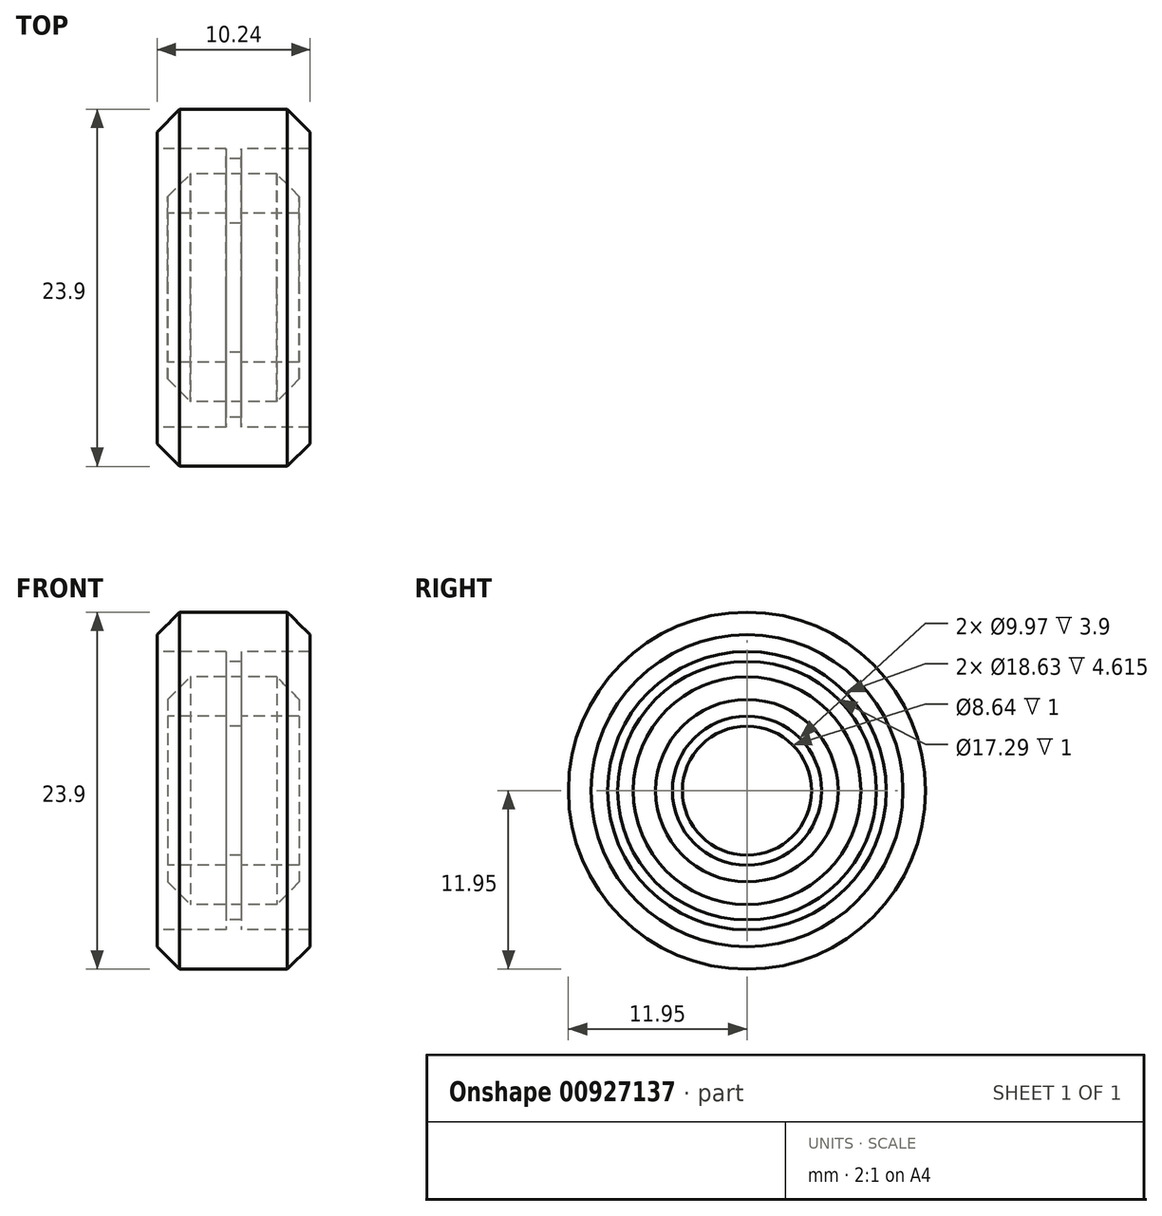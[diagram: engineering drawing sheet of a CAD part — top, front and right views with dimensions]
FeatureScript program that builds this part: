
annotation { "Feature Type Name" : "Feature", "Feature Type Description" : "" }
export const myFeature = defineFeature(function(context is Context, id is Id, definition is map)
    precondition{}
    {
        {
            var Q0;
            Q0=qCreatedBy(makeId("Top.planeOp"),FACE);
            var sketch = newSketch(context, id + "F0", { "sketchPlane" : qUnion([Q0])});
            skLineSegment(sketch, "E0", {"start": v(0, 0) * mm, "end": v(0, 4.32) * mm, "construction": true});
            skLineSegment(sketch, "E1", {"start": v(0, 4.32) * mm, "end": v(0.5, 4.32) * mm});
            skLineSegment(sketch, "E2", {"start": v(0.5, 4.32) * mm, "end": v(0.5, 4.99) * mm});
            skLineSegment(sketch, "E3", {"start": v(0.5, 4.99) * mm, "end": v(4.4, 4.99) * mm});
            skLineSegment(sketch, "E4", {"start": v(4.4, 4.99) * mm, "end": v(4.4, 6.1) * mm});
            skLineSegment(sketch, "E5", {"start": v(4.4, 6.1) * mm, "end": v(2.89, 7.62) * mm});
            skLineSegment(sketch, "E6", {"start": v(2.89, 7.62) * mm, "end": v(0, 7.62) * mm});
            skLineSegment(sketch, "E7.MirrorCS", {"start": v(0, 4.32) * mm, "end": v(-0.5, 4.32) * mm});
            skLineSegment(sketch, "E8.MirrorCS", {"start": v(-4.4, 6.1) * mm, "end": v(-2.89, 7.62) * mm});
            skLineSegment(sketch, "E9.MirrorCS", {"start": v(-0.5, 4.32) * mm, "end": v(-0.5, 4.99) * mm});
            skLineSegment(sketch, "E10.MirrorCS", {"start": v(-0.5, 4.99) * mm, "end": v(-4.4, 4.99) * mm});
            skLineSegment(sketch, "E11.MirrorCS", {"start": v(-2.89, 7.62) * mm, "end": v(0, 7.62) * mm});
            skLineSegment(sketch, "E12.MirrorCS", {"start": v(-4.4, 4.99) * mm, "end": v(-4.4, 6.1) * mm});
            skLineSegment(sketch, "E13", {"start": v(0, 0) * mm, "end": v(4.58, 0) * mm, "construction": true});
            skSolve(sketch);
        }
        {
            var Q0;
            Q0=qCreatedBy(makeId("Top.planeOp"),FACE);
            var sketch = newSketch(context, id + "F1", { "sketchPlane" : qUnion([Q0])});
            skLineSegment(sketch, "E14", {"start": v(0, 0) * mm, "end": v(0, 8.65) * mm, "construction": true});
            skLineSegment(sketch, "E15", {"start": v(0, 8.65) * mm, "end": v(0.5, 8.65) * mm});
            skLineSegment(sketch, "E16", {"start": v(0.5, 8.65) * mm, "end": v(0.5, 9.31) * mm});
            skLineSegment(sketch, "E17", {"start": v(0.5, 9.31) * mm, "end": v(5.11, 9.31) * mm});
            skLineSegment(sketch, "E18", {"start": v(5.12, 9.31) * mm, "end": v(5.12, 10.43) * mm});
            skLineSegment(sketch, "E19", {"start": v(5.12, 10.43) * mm, "end": v(3.6, 11.95) * mm});
            skLineSegment(sketch, "E20", {"start": v(0, 0) * mm, "end": v(4.42, 0) * mm, "construction": true});
            skLineSegment(sketch, "E21", {"start": v(3.6, 11.95) * mm, "end": v(0, 11.95) * mm});
            skLineSegment(sketch, "E22", {"start": v(0, 0) * mm, "end": v(0, 11.95) * mm, "construction": true});
            skLineSegment(sketch, "E23.MirrorCS", {"start": v(-0.5, 8.65) * mm, "end": v(-0.5, 9.31) * mm});
            skLineSegment(sketch, "E24.MirrorCS", {"start": v(0, 8.65) * mm, "end": v(-0.5, 8.65) * mm});
            skLineSegment(sketch, "E25.MirrorCS", {"start": v(-3.6, 11.95) * mm, "end": v(0, 11.95) * mm});
            skLineSegment(sketch, "E26.MirrorCS", {"start": v(-5.12, 9.31) * mm, "end": v(-5.12, 10.43) * mm});
            skLineSegment(sketch, "E27.MirrorCS", {"start": v(-5.12, 10.43) * mm, "end": v(-3.6, 11.95) * mm});
            skLineSegment(sketch, "E28.MirrorCS", {"start": v(-0.5, 9.31) * mm, "end": v(-5.12, 9.31) * mm});
            skLineSegment(sketch, "E29", {"start": v(-5.12, 9.31) * mm, "end": v(5.11, 9.31) * mm, "construction": true});
            skSolve(sketch);
        }
        {
            var Q0;
            Q0=makeQuery(id+"F0.imprint","IMPRINT",FACE,{"disambiguationData":[TD([[makeQuery(id+"F0.imprint","IMPRINT",EDGE,{"derivedFrom":sQuery(id+"F0.wireOp",EDGE,"E1")}),1.0]])]});
            var Q1;
            Q1=sQuery(id+"F0.wireOp",EDGE,"E13");
            revolve(context, id + "F2", {"surfaceOperationType" : NewSurfaceOperationType.NEW, "entities" : qUnion([Q0]), "axis" : qUnion([Q1]), "revolveType" : RevolveType.FULL});
        }
        {
            var Q0;
            Q0=makeQuery(id+"F1.imprint","IMPRINT",FACE,{"disambiguationData":[TD([[makeQuery(id+"F1.imprint","IMPRINT",EDGE,{"derivedFrom":sQuery(id+"F1.wireOp",EDGE,"E15")}),1.0]])]});
            var Q1;
            Q1=sQuery(id+"F1.wireOp",EDGE,"E20");
            revolve(context, id + "F3", {"surfaceOperationType" : NewSurfaceOperationType.NEW, "entities" : qUnion([Q0]), "axis" : qUnion([Q1]), "revolveType" : RevolveType.FULL});
        }
    });
